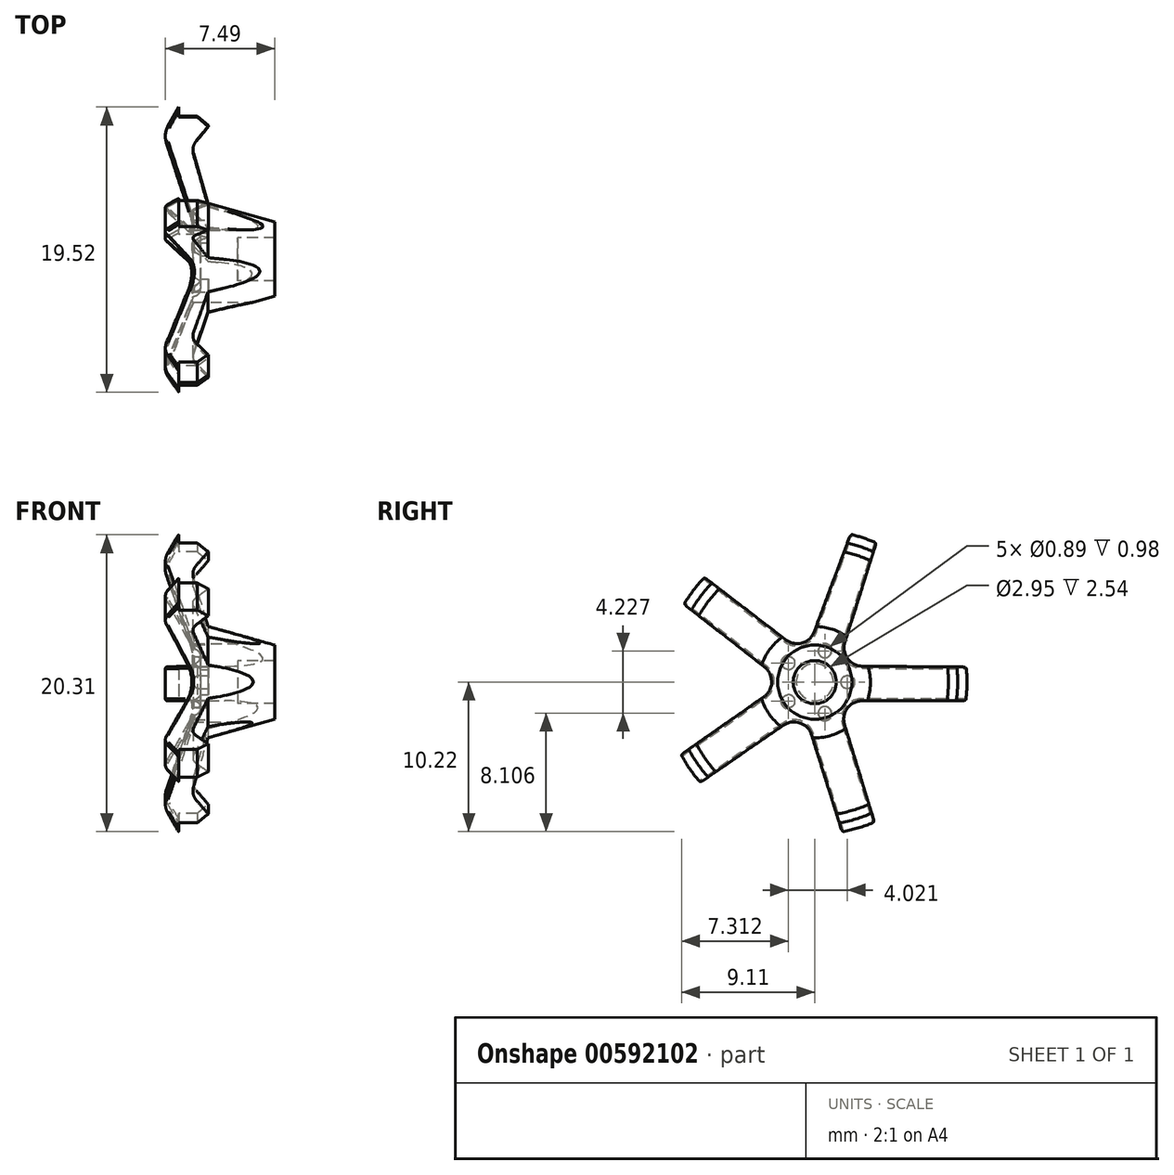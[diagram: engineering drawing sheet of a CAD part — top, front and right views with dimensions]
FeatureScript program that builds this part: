
annotation { "Feature Type Name" : "Feature", "Feature Type Description" : "" }
export const myFeature = defineFeature(function(context is Context, id is Id, definition is map)
    precondition{}
    {
        {
            var Q0;
            Q0=qCreatedBy(makeId("Front.planeOp"),FACE);
            var sketch = newSketch(context, id + "F0", { "sketchPlane" : qUnion([Q0])});
            skLineSegment(sketch, "E0", {"start": v(-5.6, 0) * mm, "end": v(-5.6, 1.48) * mm});
            skLineSegment(sketch, "E1", {"start": v(-5.6, 1.48) * mm, "end": v(-3.06, 1.48) * mm});
            skLineSegment(sketch, "E2", {"start": v(-3.06, 1.48) * mm, "end": v(-3.06, 2.54) * mm});
            skLineSegment(sketch, "E3", {"start": v(-3.06, 2.54) * mm, "end": v(-7.63, 3.8) * mm});
            skLineSegment(sketch, "E4", {"start": v(-7.63, 3.8) * mm, "end": v(-8.63, 7.24) * mm});
            skLineSegment(sketch, "E5", {"start": v(-8.43, 8.17) * mm, "end": v(-7.62, 9.14) * mm});
            skLineSegment(sketch, "E6", {"start": v(-7.62, 9.14) * mm, "end": v(-8.38, 9.78) * mm});
            skLineSegment(sketch, "E7", {"start": v(-8.38, 9.78) * mm, "end": v(-9.65, 9.78) * mm});
            skLineSegment(sketch, "E8", {"start": v(-9.65, 9.78) * mm, "end": v(-9.65, 10.41) * mm});
            skLineSegment(sketch, "E9", {"start": v(-9.65, 10.41) * mm, "end": v(-10.4, 9.08) * mm});
            skLineSegment(sketch, "E10", {"start": v(-10.49, 8.06) * mm, "end": v(-8.65, 2.54) * mm});
            skLineSegment(sketch, "E11", {"start": v(-8.65, 2.54) * mm, "end": v(-8.65, 2.54) * mm});
            skLineSegment(sketch, "E12", {"start": v(-8.14, 2.03) * mm, "end": v(-8.14, 1.78) * mm});
            skLineSegment(sketch, "E13", {"start": v(-8.65, 1.27) * mm, "end": v(-8.65, 1.27) * mm});
            skLineSegment(sketch, "E14", {"start": v(-8.65, 1.27) * mm, "end": v(-8.65, 0) * mm});
            skLineSegment(sketch, "E15", {"start": v(-8.65, 0) * mm, "end": v(-5.6, 0) * mm});
            skPoint(sketch, "E16.visualSharp", {"position": v(-8.14, 1.27) * mm});
            skArc(sketch, "E16.filletArc", {"start": v(-8.65, 1.27) * mm, "mid": v(-8.29, 1.42) * mm, "end": v(-8.14, 1.78) * mm});
            skPoint(sketch, "E17.visualSharp", {"position": v(-8.14, 2.54) * mm});
            skArc(sketch, "E17.filletArc", {"start": v(-8.14, 2.03) * mm, "mid": v(-8.29, 2.4) * mm, "end": v(-8.65, 2.54) * mm});
            skPoint(sketch, "E18.visualSharp", {"position": v(-10.67, 8.59) * mm});
            skArc(sketch, "E18.filletArc", {"start": v(-10.4, 9.08) * mm, "mid": v(-10.55, 8.58) * mm, "end": v(-10.49, 8.06) * mm});
            skPoint(sketch, "E19.visualSharp", {"position": v(-8.78, 7.75) * mm});
            skArc(sketch, "E19.filletArc", {"start": v(-8.43, 8.17) * mm, "mid": v(-8.65, 7.73) * mm, "end": v(-8.63, 7.24) * mm});
            skSolve(sketch);
        }
        {
            var Q0;
            Q0 = qSketchRegion(id + "F0", true);
            var Q1;
            Q1=sQuery(id+"F0.wireOp",EDGE,"E15");
            revolve(context, id + "F1", {"entities" : qUnion([Q0]), "axis" : qUnion([Q1]), "revolveType" : RevolveType.FULL});
        }
        {
            var Q0;
            Q0=qCreatedBy(makeId("Right.planeOp"),FACE);
            cPlane(context, id + "F2", {"entities" : qUnion([Q0]), "cplaneType" : CPlaneType.OFFSET, "offset" : 7.62 * mm, "oppositeDirection" : true, "width" : 152.4 * mm, "height" : 152.4 * mm});
        }
        {
            var Q0;
            Q0=qCreatedBy(id+"F2.planeOp",FACE);
            var sketch = newSketch(context, id + "F3", { "sketchPlane" : qUnion([Q0])});
            skCircle(sketch, "E20", {"center": v(2.22, 0) * mm, "radius": 0.44 * mm});
            skCircle(sketch, "E21.1.0", {"center": v(0.69, 2.11) * mm, "radius": 0.44 * mm});
            skCircle(sketch, "E21.2.0", {"center": v(-1.8, 1.3) * mm, "radius": 0.44 * mm});
            skCircle(sketch, "E21.3.0", {"center": v(-1.8, -1.3) * mm, "radius": 0.44 * mm});
            skCircle(sketch, "E21.4.0", {"center": v(0.69, -2.11) * mm, "radius": 0.44 * mm});
            skPoint(sketch, "E21.center", {"position": v(0, 0) * mm});
            skSolve(sketch);
        }
        {
            var Q0;
            Q0 = qSketchRegion(id + "F3", true);
            extrude(context, id + "F4", {"entities" : qUnion([Q0]), "operationType" : NewBodyOperationType.REMOVE, "endBound" : BoundingType.THROUGH_ALL, "oppositeDirection" : true, "depth" : 25.4 * mm, "offsetDistance" : 25.4 * mm});
        }
        {
            var Q0;
            Q0=qCreatedBy(makeId("Right.planeOp"),FACE);
            var sketch = newSketch(context, id + "F5", { "sketchPlane" : qUnion([Q0])});
            skLineSegment(sketch, "E22", {"start": v(3.26, 1.09) * mm, "end": v(10.84, 1.03) * mm});
            skLineSegment(sketch, "E23.MirrorCS", {"start": v(2.06, 2.74) * mm, "end": v(4.35, 9.97) * mm});
            skArc(sketch, "E24", {"start": v(10.84, 1.03) * mm, "mid": v(8.77, 6.35) * mm, "end": v(4.35, 9.97) * mm});
            skPoint(sketch, "E25.visualSharp", {"position": v(1.54, 1.1) * mm});
            skArc(sketch, "E25.filletArc", {"start": v(2.06, 2.74) * mm, "mid": v(2.25, 1.61) * mm, "end": v(3.26, 1.09) * mm});
            skLineSegment(sketch, "E26.1.0", {"start": v(2.04, -2.91) * mm, "end": v(4.26, -10.16) * mm});
            skArc(sketch, "E26.1.1", {"start": v(3.25, -1.27) * mm, "mid": v(2.23, -1.79) * mm, "end": v(2.04, -2.91) * mm});
            skLineSegment(sketch, "E26.1.2", {"start": v(3.25, -1.27) * mm, "end": v(10.83, -1.28) * mm});
            skArc(sketch, "E26.1.3", {"start": v(4.26, -10.16) * mm, "mid": v(8.72, -6.58) * mm, "end": v(10.83, -1.28) * mm});
            skLineSegment(sketch, "E26.2.0", {"start": v(-2.15, -2.95) * mm, "end": v(-8.4, -7.25) * mm});
            skArc(sketch, "E26.2.1", {"start": v(-0.21, -3.61) * mm, "mid": v(-1.01, -2.8) * mm, "end": v(-2.15, -2.95) * mm});
            skLineSegment(sketch, "E26.2.2", {"start": v(-0.21, -3.61) * mm, "end": v(2.06, -10.85) * mm});
            skArc(sketch, "E26.2.3", {"start": v(-8.4, -7.25) * mm, "mid": v(-3.64, -10.42) * mm, "end": v(2.06, -10.85) * mm});
            skLineSegment(sketch, "E26.3.0", {"start": v(-3.44, 1.03) * mm, "end": v(-9.42, 5.7) * mm});
            skArc(sketch, "E26.3.1", {"start": v(-3.5, -1) * mm, "mid": v(-2.95, 0) * mm, "end": v(-3.44, 1.03) * mm});
            skLineSegment(sketch, "E26.3.2", {"start": v(-3.5, -1) * mm, "end": v(-9.7, -5.35) * mm});
            skArc(sketch, "E26.3.3", {"start": v(-9.42, 5.7) * mm, "mid": v(-11.01, 0.2) * mm, "end": v(-9.7, -5.35) * mm});
            skLineSegment(sketch, "E26.4.0", {"start": v(-0.03, 3.46) * mm, "end": v(2.62, 10.57) * mm});
            skArc(sketch, "E26.4.1", {"start": v(-2, 2.9) * mm, "mid": v(-0.87, 2.68) * mm, "end": v(-0.03, 3.46) * mm});
            skLineSegment(sketch, "E26.4.2", {"start": v(-2, 2.9) * mm, "end": v(-8, 7.52) * mm});
            skArc(sketch, "E26.4.3", {"start": v(2.62, 10.57) * mm, "mid": v(-3.1, 10.44) * mm, "end": v(-8, 7.52) * mm});
            skPoint(sketch, "E26.center", {"position": v(-0.08, -0.08) * mm});
            skLineSegment(sketch, "E26.anchor1", {"start": v(-0.08, -0.08) * mm, "end": v(-0.32, -0.25) * mm, "construction": true});
            skLineSegment(sketch, "E26.anchor2", {"start": v(-0.08, -0.08) * mm, "end": v(0, -0.36) * mm, "construction": true});
            skSolve(sketch);
        }
        {
            var Q0;
            Q0 = qSketchRegion(id + "F5", true);
            extrude(context, id + "F6", {"entities" : qUnion([Q0]), "operationType" : NewBodyOperationType.REMOVE, "endBound" : BoundingType.THROUGH_ALL, "oppositeDirection" : true, "depth" : 25.4 * mm, "offsetDistance" : 25.4 * mm});
        }
        {
            var Q0;
            Q0=makeQuery(id+"F1.opRevolve","SWEPT_FACE",FACE,{"disambiguationData":[OSD([sQuery(id+"F0.wireOp",EDGE,"E10")])]});
            var Q1;
            Q1=makeQuery(id+"F6.boolean.opBoolean","SPLIT",FACE,{"disambiguationData":[TD([makeQuery(id+"F6.opExtrude","SWEPT_FACE",FACE,{"disambiguationData":[OSD([sQuery(id+"F5.wireOp",EDGE,"E26.3.0")])]})])],"derivedFrom":makeQuery(id+"F1.opRevolve","SWEPT_FACE",FACE,{"disambiguationData":[OSD([sQuery(id+"F0.wireOp",EDGE,"E18.filletArc")])]})});
            fillet(context, id + "F7", {"entities" : qUnion([Q0, Q1]), "radius" : 0.13 * mm, "tangentPropagation" : true, "allowEdgeOverflow" : false});
        }
    });
